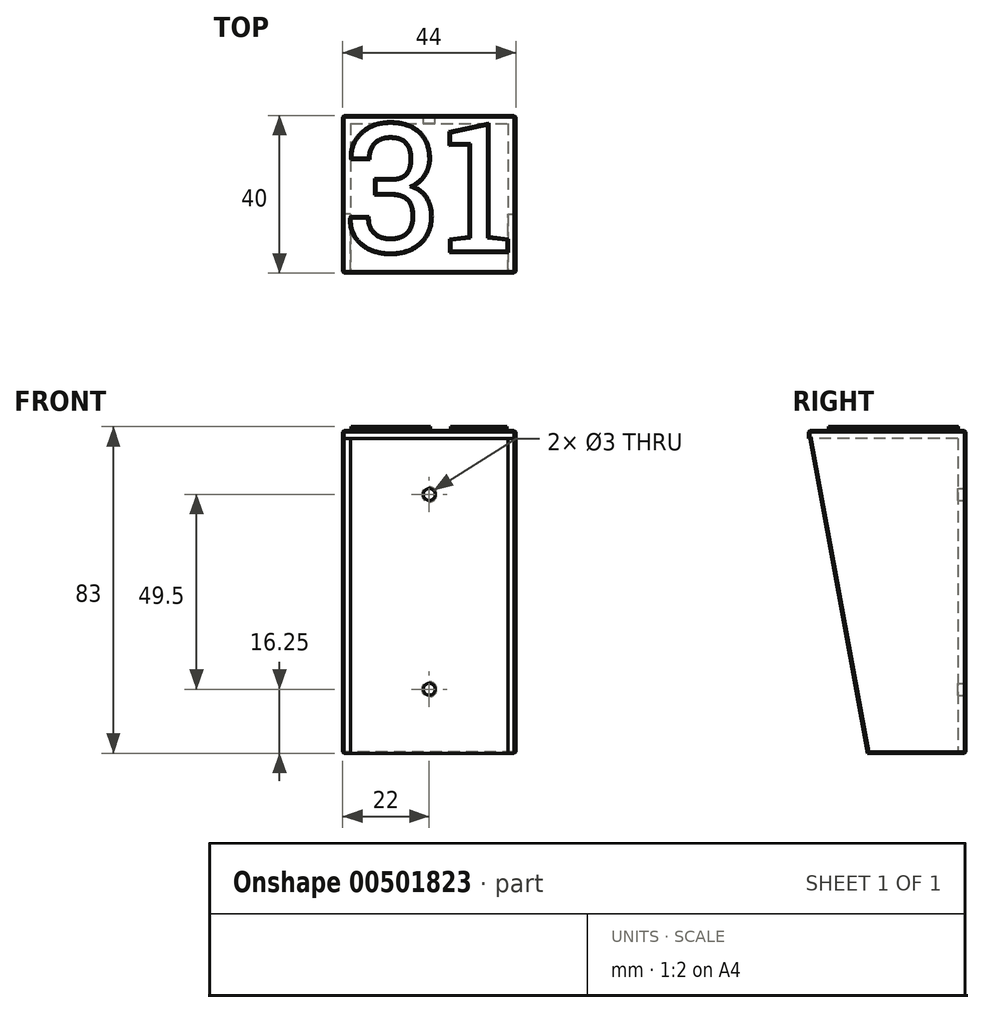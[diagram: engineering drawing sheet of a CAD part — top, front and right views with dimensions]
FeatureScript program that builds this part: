
annotation { "Feature Type Name" : "Feature", "Feature Type Description" : "" }
export const myFeature = defineFeature(function(context is Context, id is Id, definition is map)
    precondition{}
    {
        {
            var Q0;
            Q0=qCreatedBy(makeId("Front.planeOp"),FACE);
            var sketch = newSketch(context, id + "F0", { "sketchPlane" : qUnion([Q0])});
            skLineSegment(sketch, "E0.bottom", {"start": v(0, 0) * mm, "end": v(44, 0) * mm});
            skLineSegment(sketch, "E0.top", {"start": v(0, 82) * mm, "end": v(44, 82) * mm});
            skLineSegment(sketch, "E0.left", {"start": v(0, 0) * mm, "end": v(0, 82) * mm});
            skLineSegment(sketch, "E0.right", {"start": v(44, 0) * mm, "end": v(44, 82) * mm});
            skLineSegment(sketch, "E1.0", {"start": v(0, 80) * mm, "end": v(44, 80) * mm});
            skSolve(sketch);
        }
        {
            var Q0;
            Q0=qCreatedBy(makeId("Right.planeOp"),FACE);
            var sketch = newSketch(context, id + "F1", { "sketchPlane" : qUnion([Q0])});
            skLineSegment(sketch, "E2", {"start": v(0, 0) * mm, "end": v(-25, 0) * mm});
            skLineSegment(sketch, "E3", {"start": v(0, 82) * mm, "end": v(-40, 82) * mm});
            skLineSegment(sketch, "E4", {"start": v(-40, 82) * mm, "end": v(-25, 0) * mm});
            skLineSegment(sketch, "E5", {"start": v(0, 0) * mm, "end": v(0, 82) * mm});
            skLineSegment(sketch, "E6.0", {"start": v(-2, 0) * mm, "end": v(-2, 82) * mm});
            skLineSegment(sketch, "E7", {"start": v(-2, 0) * mm, "end": v(0, 0) * mm});
            skLineSegment(sketch, "E8", {"start": v(-2, 82) * mm, "end": v(0, 82) * mm});
            skSolve(sketch);
        }
        {
            var Q0;
            Q0=qCreatedBy(makeId("Right.planeOp"),FACE);
            cPlane(context, id + "F2", {"entities" : qUnion([Q0]), "cplaneType" : CPlaneType.OFFSET, "offset" : 44 * mm, "width" : 150 * mm, "height" : 150 * mm});
        }
        {
            var Q0;
            Q0=qCreatedBy(id+"F2.planeOp",FACE);
            var sketch = newSketch(context, id + "F3", { "sketchPlane" : qUnion([Q0])});
            skLineSegment(sketch, "E9.0", {"start": v(0, 82) * mm, "end": v(-40, 82) * mm});
            skLineSegment(sketch, "E10.0", {"start": v(-40, 82) * mm, "end": v(-25, 0) * mm});
            skLineSegment(sketch, "E11.0", {"start": v(0, 0) * mm, "end": v(-25, 0) * mm});
            skLineSegment(sketch, "E12.0", {"start": v(0, 0) * mm, "end": v(0, 82) * mm});
            skLineSegment(sketch, "E13.0", {"start": v(-2, 0) * mm, "end": v(-2, 82) * mm});
            skLineSegment(sketch, "E14.0", {"start": v(0, 80) * mm, "end": v(-39.63, 80) * mm});
            skSolve(sketch);
        }
        {
            var Q0;
            Q0=makeQuery(id+"F1.imprint","IMPRINT",FACE,{"disambiguationData":[TD([[makeQuery(id+"F1.imprint","IMPRINT",EDGE,{"derivedFrom":sQuery(id+"F1.wireOp",EDGE,"E2")}),-1.0]])]});
            extrude(context, id + "F4", {"entities" : qUnion([Q0]), "depth" : 2 * mm});
        }
        {
            var Q0;
            {var subQ0=sQuery(id+"F3.wireOp",EDGE,"E10.0");Q0=makeQuery(id+"F3.imprint","IMPRINT",FACE,{"disambiguationData":[TD([[makeQuery(id+"F3.imprint","IMPRINT",EDGE,{"derivedFrom":subQ0}),1.0]])]});}
            extrude(context, id + "F5", {"entities" : qUnion([Q0]), "oppositeDirection" : true, "depth" : 2 * mm});
        }
        {
            var Q0;
            {var subQ0=sQuery(id+"F0.wireOp",EDGE,"E0.bottom");Q0=makeQuery(id+"F0.imprint","IMPRINT",FACE,{"disambiguationData":[TD([[makeQuery(id+"F0.imprint","IMPRINT",EDGE,{"derivedFrom":subQ0}),1.0]])]});}
            extrude(context, id + "F6", {"entities" : qUnion([Q0]), "depth" : 2 * mm});
        }
        {
            var Q0;
            {var subQ0=sQuery(id+"F0.wireOp",EDGE,"E0.top");Q0=makeQuery(id+"F0.imprint","IMPRINT",FACE,{"disambiguationData":[TD([[makeQuery(id+"F0.imprint","IMPRINT",EDGE,{"derivedFrom":subQ0}),-1.0]])]});}
            extrude(context, id + "F7", {"entities" : qUnion([Q0]), "operationType" : NewBodyOperationType.ADD, "depth" : 40 * mm});
        }
        {
            var Q0;
            {var subQ0=sQuery(id+"F0.wireOp",EDGE,"E1.0");var subQ1=sQuery(id+"F0.wireOp",EDGE,"E0.right");var subQ2=sQuery(id+"F0.wireOp",EDGE,"E0.left");Q0=makeQuery(id+"F7.boolean.opBoolean","MERGE",FACE,{"derivedFrom":[makeQuery(id+"F6.opExtrude","CAP_FACE",FACE,{"disambiguationData":[OSD([sQuery(id+"F0.wireOp",EDGE,"E0.bottom"),subQ2,subQ1,subQ0])],"isStart":true}),makeQuery(id+"F7.opExtrude","CAP_FACE",FACE,{"disambiguationData":[OSD([sQuery(id+"F0.wireOp",EDGE,"E0.top"),subQ2,subQ1,subQ0])],"isStart":true})]});}
            var sketch = newSketch(context, id + "F8", { "sketchPlane" : qUnion([Q0])});
            skLineSegment(sketch, "E15", {"start": v(-22, 82) * mm, "end": v(-22, 0) * mm, "construction": true});
            skCircle(sketch, "E16", {"center": v(-22, 65.75) * mm, "radius": 1.5 * mm});
            skLineSegment(sketch, "E17", {"start": v(-44, 41) * mm, "end": v(0, 41) * mm, "construction": true});
            skCircle(sketch, "E18.MirrorC", {"center": v(-22, 16.25) * mm, "radius": 1.5 * mm});
            skSolve(sketch);
        }
        {
            var Q0;
            Q0 = qSketchRegion(id + "F8", true);
            extrude(context, id + "F9", {"entities" : qUnion([Q0]), "operationType" : NewBodyOperationType.REMOVE, "oppositeDirection" : true, "depth" : 25 * mm});
        }
        {
            var Q0;
            Q0=makeQuery(id+"F7.boolean.opBoolean","MERGE",FACE,{"derivedFrom":[makeQuery(id+"F4.opExtrude","SWEPT_FACE",FACE,{"disambiguationData":[OSD([sQuery(id+"F1.wireOp",EDGE,"E3")])]}),makeQuery(id+"F5.opExtrude","SWEPT_FACE",FACE,{"disambiguationData":[OSD([sQuery(id+"F3.wireOp",EDGE,"E9.0")])]}),makeQuery(id+"F7.opExtrude","SWEPT_FACE",FACE,{"disambiguationData":[OSD([sQuery(id+"F0.wireOp",EDGE,"E0.top")])]})]});
            var sketch = newSketch(context, id + "F10", { "sketchPlane" : qUnion([Q0])});
            skText(sketch, "E19", { "text": "31", "fontName": "RobotoSlab-Regular.ttf"});
            const initialGuessF10  = {"E19": [0.0005, -0.03444, 1, 0, 0.03244]};
            skSetInitialGuess(sketch, initialGuessF10);
            skSolve(sketch);
        }
        {
            var Q0;
            Q0 = qSketchRegion(id + "F10", true);
            var Q1;
            Q1=makeQuery(id+"F10.imprint","IMPRINT",FACE,{"disambiguationData":[TD([[makeQuery(id+"F10.imprint","IMPRINT",EDGE,{"derivedFrom":sQuery(id+"F10.wireOp",EDGE,"E19.sketch_text.stroke-0")}),-1.0]])]});
            extrude(context, id + "F11", {"entities" : qUnion([Q0, Q1]), "operationType" : NewBodyOperationType.ADD, "depth" : 1 * mm});
        }
        {
            var Q0;
            {var subQ0=sQuery(id+"F0.wireOp",EDGE,"E0.right");Q0=makeQuery(id+"F7.boolean.opBoolean","MERGE",FACE,{"derivedFrom":[makeQuery(id+"F5.opExtrude","CAP_FACE",FACE,{"disambiguationData":[OSD([sQuery(id+"F3.wireOp",EDGE,"E9.0"),sQuery(id+"F3.wireOp",EDGE,"E10.0"),sQuery(id+"F3.wireOp",EDGE,"E11.0"),sQuery(id+"F3.wireOp",EDGE,"E13.0")])],"isStart":true}),makeQuery(id+"F6.opExtrude","SWEPT_FACE",FACE,{"disambiguationData":[OSD([subQ0])]}),makeQuery(id+"F7.opExtrude","SWEPT_FACE",FACE,{"disambiguationData":[OSD([subQ0])]})]});}
            var Q1;
            Q1=makeQuery(id+"F7.boolean.opBoolean","MERGE",FACE,{"derivedFrom":[makeQuery(id+"F4.opExtrude","SWEPT_FACE",FACE,{"disambiguationData":[OSD([sQuery(id+"F1.wireOp",EDGE,"E3")])]}),makeQuery(id+"F5.opExtrude","SWEPT_FACE",FACE,{"disambiguationData":[OSD([sQuery(id+"F3.wireOp",EDGE,"E9.0")])]}),makeQuery(id+"F7.opExtrude","SWEPT_FACE",FACE,{"disambiguationData":[OSD([sQuery(id+"F0.wireOp",EDGE,"E0.top")])]})]});
            var Q2;
            {var subQ0=sQuery(id+"F0.wireOp",EDGE,"E1.0");var subQ1=sQuery(id+"F0.wireOp",EDGE,"E0.right");var subQ2=sQuery(id+"F0.wireOp",EDGE,"E0.left");Q2=makeQuery(id+"F7.boolean.opBoolean","MERGE",FACE,{"derivedFrom":[makeQuery(id+"F6.opExtrude","CAP_FACE",FACE,{"disambiguationData":[OSD([sQuery(id+"F0.wireOp",EDGE,"E0.bottom"),subQ2,subQ1,subQ0])],"isStart":true}),makeQuery(id+"F7.opExtrude","CAP_FACE",FACE,{"disambiguationData":[OSD([sQuery(id+"F0.wireOp",EDGE,"E0.top"),subQ2,subQ1,subQ0])],"isStart":true})]});}
            var Q3;
            {var subQ0=sQuery(id+"F0.wireOp",EDGE,"E0.left");Q3=makeQuery(id+"F7.boolean.opBoolean","MERGE",FACE,{"derivedFrom":[makeQuery(id+"F4.opExtrude","CAP_FACE",FACE,{"disambiguationData":[OSD([sQuery(id+"F1.wireOp",EDGE,"E2"),sQuery(id+"F1.wireOp",EDGE,"E3"),sQuery(id+"F1.wireOp",EDGE,"E4"),sQuery(id+"F1.wireOp",EDGE,"E6.0")])],"isStart":true}),makeQuery(id+"F6.opExtrude","SWEPT_FACE",FACE,{"disambiguationData":[OSD([subQ0])]}),makeQuery(id+"F7.opExtrude","SWEPT_FACE",FACE,{"disambiguationData":[OSD([subQ0])]})]});}
            chamfer(context, id + "F12", {"entities" : qUnion([Q0, Q1, Q2, Q3]), "width" : 0.4 * mm, "tangentPropagation" : true});
        }
    });
